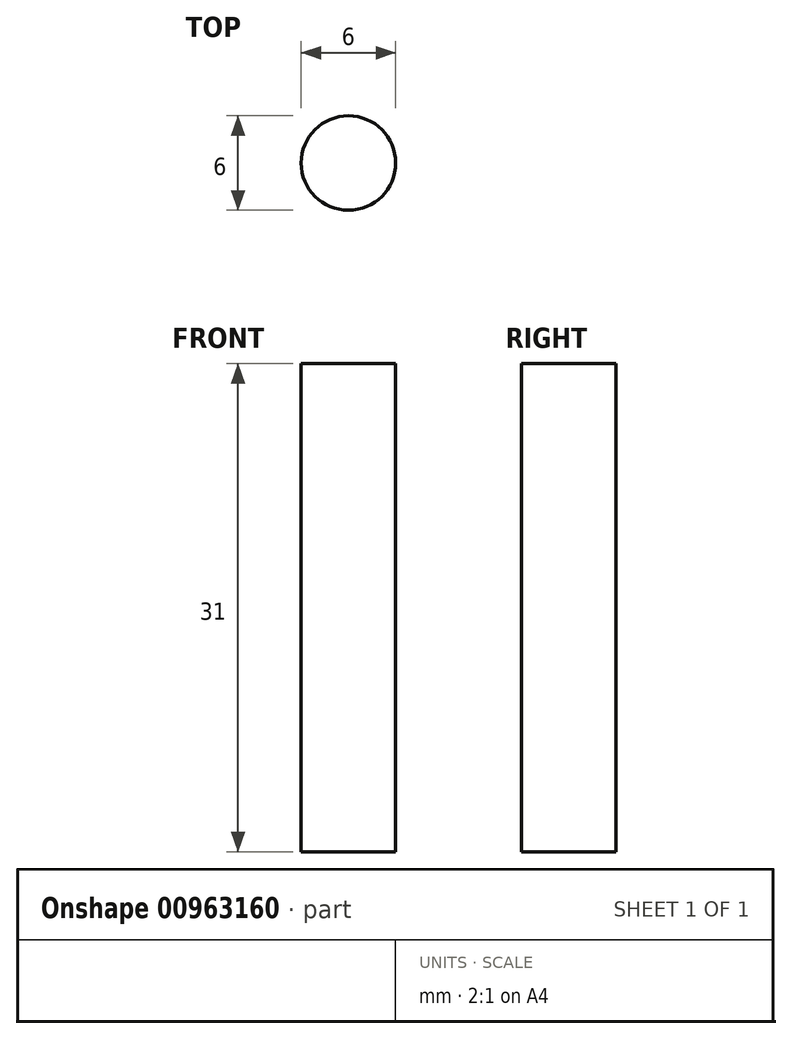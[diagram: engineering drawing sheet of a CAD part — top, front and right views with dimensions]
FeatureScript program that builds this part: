
annotation { "Feature Type Name" : "Feature", "Feature Type Description" : "" }
export const myFeature = defineFeature(function(context is Context, id is Id, definition is map)
    precondition{}
    {
        {
            var Q0;
            Q0=qCreatedBy(makeId("Top.planeOp"),FACE);
            var sketch = newSketch(context, id + "F0", { "sketchPlane" : qUnion([Q0])});
            skCircle(sketch, "E0", {"center": v(0, 0) * mm, "radius": 3 * mm});
            skSolve(sketch);
        }
        {
            var Q0;
            Q0=makeQuery(id+"F0.imprint","IMPRINT",FACE,{"disambiguationData":[TD([[makeQuery(id+"F0.imprint","IMPRINT",EDGE,{"derivedFrom":sQuery(id+"F0.wireOp",EDGE,"E0")}),1.0]])]});
            extrude(context, id + "F1", {"entities" : qUnion([Q0]), "depth" : 31 * mm, "offsetDistance" : 25 * mm});
        }
    });
